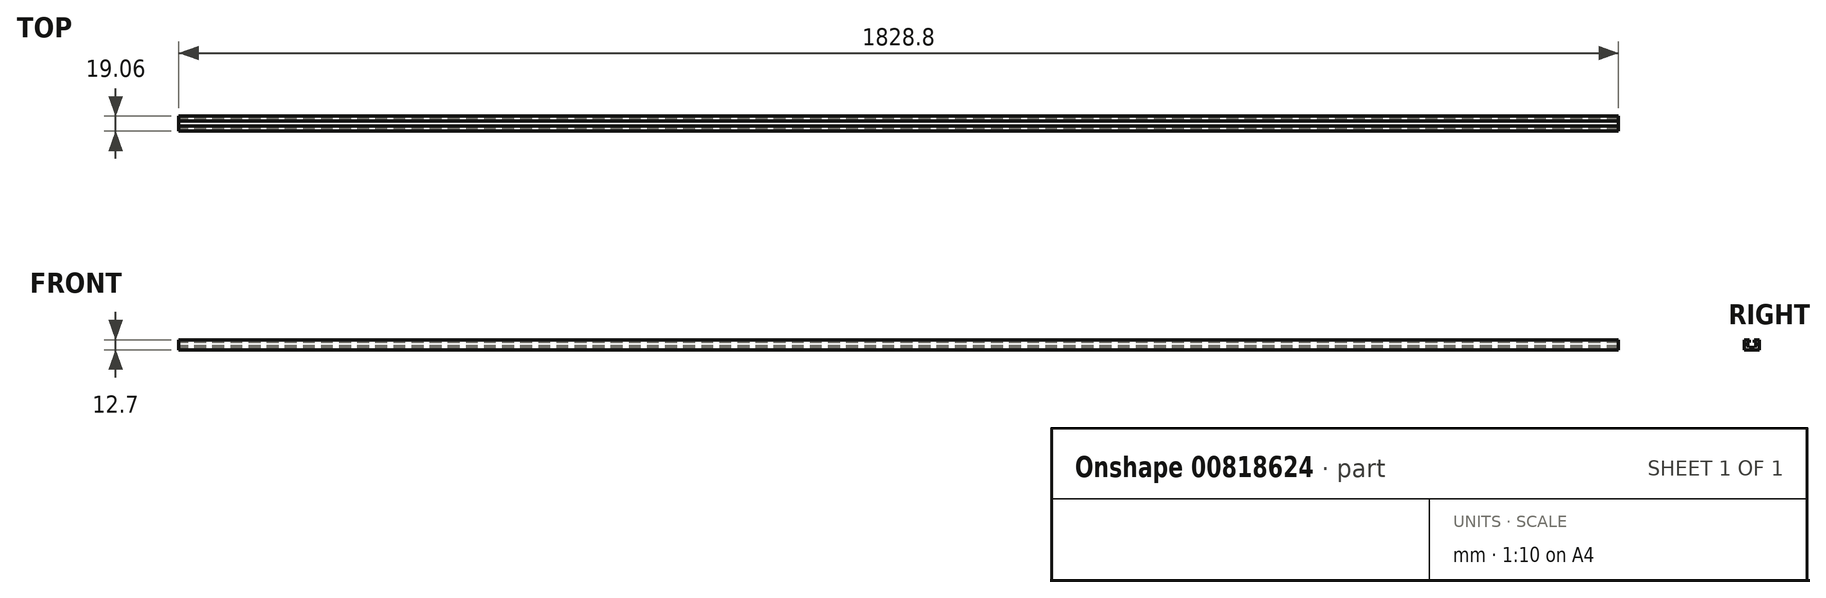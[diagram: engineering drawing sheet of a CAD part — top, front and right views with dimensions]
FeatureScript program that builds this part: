
annotation { "Feature Type Name" : "Feature", "Feature Type Description" : "" }
export const myFeature = defineFeature(function(context is Context, id is Id, definition is map)
    precondition{}
    {
        {
            var Q0;
            Q0=qCreatedBy(makeId("Right.planeOp"),FACE);
            var sketch = newSketch(context, id + "F0", { "sketchPlane" : qUnion([Q0])});
            skLineSegment(sketch, "E0.bottom", {"start": v(-9.53, -6.35) * mm, "end": v(9.53, -6.35) * mm});
            skLineSegment(sketch, "E0.top", {"start": v(-9.53, 6.35) * mm, "end": v(-3.18, 6.35) * mm});
            skLineSegment(sketch, "E0.left", {"start": v(-9.53, -6.35) * mm, "end": v(-9.53, 6.35) * mm});
            skLineSegment(sketch, "E0.right", {"start": v(9.53, -6.35) * mm, "end": v(9.53, 6.35) * mm});
            skPoint(sketch, "E0.middle", {"position": v(0, 0) * mm});
            skLineSegment(sketch, "E1.top", {"start": v(-3.17, -3.18) * mm, "end": v(3.18, -3.18) * mm});
            skLineSegment(sketch, "E1.left", {"start": v(-3.18, 6.35) * mm, "end": v(-3.17, 3.18) * mm});
            skLineSegment(sketch, "E1.right", {"start": v(3.17, 6.35) * mm, "end": v(3.17, 3.18) * mm});
            skLineSegment(sketch, "E2.trimOffspring", {"start": v(3.17, 6.35) * mm, "end": v(9.53, 6.35) * mm});
            skLineSegment(sketch, "E3.bottom", {"start": v(-3.17, 3.18) * mm, "end": v(-6.35, 3.17) * mm});
            skLineSegment(sketch, "E3.top", {"start": v(-3.17, -1.59) * mm, "end": v(-6.35, -1.59) * mm});
            skLineSegment(sketch, "E3.right", {"start": v(-6.35, 3.17) * mm, "end": v(-6.35, -1.59) * mm});
            skLineSegment(sketch, "E4.trimOffspring", {"start": v(-3.17, -1.59) * mm, "end": v(-3.17, -3.18) * mm});
            skLineSegment(sketch, "E5.bottom", {"start": v(3.17, 3.18) * mm, "end": v(6.35, 3.18) * mm});
            skLineSegment(sketch, "E5.top", {"start": v(3.17, -1.59) * mm, "end": v(6.35, -1.59) * mm});
            skLineSegment(sketch, "E5.right", {"start": v(6.35, 3.18) * mm, "end": v(6.35, -1.59) * mm});
            skLineSegment(sketch, "E6.trimOffspring", {"start": v(3.18, -1.59) * mm, "end": v(3.18, -3.18) * mm});
            skSolve(sketch);
        }
        {
            var Q0;
            Q0 = qSketchRegion(id + "F0", true);
            extrude(context, id + "F1", {"entities" : qUnion([Q0]), "depth" : 1828.8 * mm, "offsetDistance" : 25.4 * mm});
        }
    });
